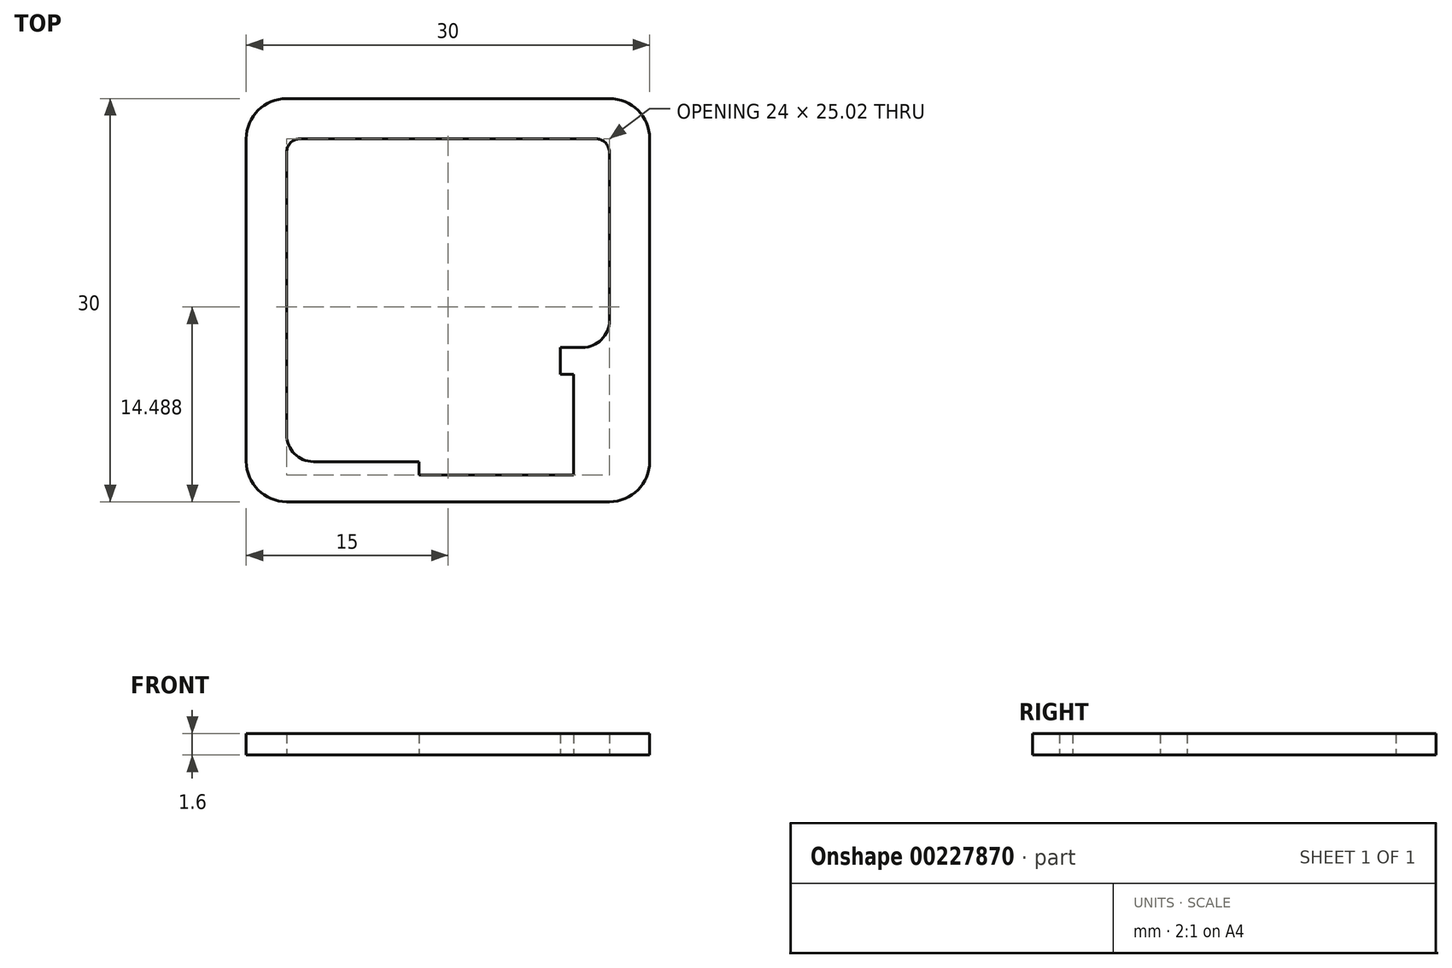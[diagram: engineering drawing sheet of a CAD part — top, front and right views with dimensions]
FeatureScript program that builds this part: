
annotation { "Feature Type Name" : "Feature", "Feature Type Description" : "" }
export const myFeature = defineFeature(function(context is Context, id is Id, definition is map)
    precondition{}
    {
        {
            var Q0;
            Q0=qCreatedBy(makeId("Top.planeOp"),FACE);
            var sketch = newSketch(context, id + "F0", { "sketchPlane" : qUnion([Q0])});
            skLineSegment(sketch, "E0.bottom", {"start": v(12, 15) * mm, "end": v(-12, 15) * mm});
            skLineSegment(sketch, "E0.top", {"start": v(12, -15) * mm, "end": v(-12, -15) * mm});
            skLineSegment(sketch, "E0.left", {"start": v(15, 12) * mm, "end": v(15, -12) * mm});
            skLineSegment(sketch, "E0.right", {"start": v(-15, 12) * mm, "end": v(-15, -12) * mm});
            skPoint(sketch, "E0.middle", {"position": v(0, 0) * mm});
            skPoint(sketch, "E1.visualSharp", {"position": v(-15, 15) * mm});
            skArc(sketch, "E1.filletArc", {"start": v(-12, 15) * mm, "mid": v(-14.12, 14.12) * mm, "end": v(-15, 12) * mm});
            skPoint(sketch, "E2.visualSharp", {"position": v(15, 15) * mm});
            skArc(sketch, "E2.filletArc", {"start": v(15, 12) * mm, "mid": v(14.12, 14.12) * mm, "end": v(12, 15) * mm});
            skPoint(sketch, "E3.visualSharp", {"position": v(15, -15) * mm});
            skArc(sketch, "E3.filletArc", {"start": v(12, -15) * mm, "mid": v(14.12, -14.12) * mm, "end": v(15, -12) * mm});
            skPoint(sketch, "E4.visualSharp", {"position": v(-15, -15) * mm});
            skArc(sketch, "E4.filletArc", {"start": v(-15, -12) * mm, "mid": v(-14.12, -14.12) * mm, "end": v(-12, -15) * mm});
            skPoint(sketch, "E5.middle", {"position": v(0, -0.17) * mm});
            skLineSegment(sketch, "E6.bottom", {"start": v(-2.15, -13.03) * mm, "end": v(9.35, -13.03) * mm});
            skLineSegment(sketch, "E6.top", {"start": v(8.35, -5.53) * mm, "end": v(9.35, -5.53) * mm});
            skLineSegment(sketch, "E6.left", {"start": v(-2.15, -13.03) * mm, "end": v(-2.15, -12.03) * mm});
            skLineSegment(sketch, "E6.right", {"start": v(9.35, -13.03) * mm, "end": v(9.35, -5.53) * mm});
            skLineSegment(sketch, "E7.bottom", {"start": v(-11, 12) * mm, "end": v(11, 12) * mm});
            skLineSegment(sketch, "E7.top", {"start": v(-10, -12.03) * mm, "end": v(-2.15, -12.03) * mm});
            skLineSegment(sketch, "E7.left", {"start": v(-12, 11) * mm, "end": v(-12, -10.03) * mm});
            skLineSegment(sketch, "E7.right", {"start": v(8.35, -3.53) * mm, "end": v(8.35, -5.53) * mm});
            skLineSegment(sketch, "E8", {"start": v(8.35, -5.53) * mm, "end": v(8.35, -3.53) * mm});
            skLineSegment(sketch, "E9", {"start": v(8.35, -3.53) * mm, "end": v(10, -3.53) * mm});
            skLineSegment(sketch, "E10", {"start": v(12, -1.53) * mm, "end": v(12, 11) * mm});
            skPoint(sketch, "E11.visualSharp", {"position": v(12, -3.53) * mm});
            skArc(sketch, "E11.filletArc", {"start": v(10, -3.53) * mm, "mid": v(11.41, -2.94) * mm, "end": v(12, -1.53) * mm});
            skPoint(sketch, "E12.visualSharp", {"position": v(-12, -12.03) * mm});
            skArc(sketch, "E12.filletArc", {"start": v(-12, -10.03) * mm, "mid": v(-11.41, -11.44) * mm, "end": v(-10, -12.03) * mm});
            skArc(sketch, "E13", {"start": v(-11, 12) * mm, "mid": v(-11.7, 11.7) * mm, "end": v(-12, 11) * mm});
            skArc(sketch, "E14", {"start": v(12, 11) * mm, "mid": v(11.7, 11.7) * mm, "end": v(11, 12) * mm});
            skSolve(sketch);
        }
        {
            var Q0;
            Q0=makeQuery(id+"F0.imprint","IMPRINT",FACE,{"disambiguationData":[TD([[makeQuery(id+"F0.imprint","IMPRINT",EDGE,{"derivedFrom":sQuery(id+"F0.wireOp",EDGE,"E0.bottom")}),1.0]])]});
            var Q1;
            Q1=makeQuery(id+"F0.imprint","IMPRINT",FACE,{"disambiguationData":[TD([[makeQuery(id+"F0.imprint","IMPRINT",EDGE,{"derivedFrom":sQuery(id+"F0.wireOp",EDGE,"37d6cbd4-4a48-45da-a80f-8b9b84353664")}),-1.0]])]});
            var Q2;
            {var subQ0=sQuery(id+"F0.wireOp",EDGE,"756c47a4-f17b-4714-afab-c32c89d008be.bottom");Q2=makeQuery(id+"F0.imprint","IMPRINT",FACE,{"disambiguationData":[TD([[makeQuery(id+"F0.imprint","IMPRINT",EDGE,{"derivedFrom":subQ0}),1.0]])]});}
            var Q3;
            {var subQ9=sQuery(id+"F0.wireOp",EDGE,"756c47a4-f17b-4714-afab-c32c89d008be.bottom");Q3=makeQuery(id+"F0.imprint","IMPRINT",FACE,{"disambiguationData":[TD([[makeQuery(id+"F0.imprint","IMPRINT",EDGE,{"derivedFrom":subQ9}),-1.0]])]});}
            extrude(context, id + "F1", {"entities" : qUnion([Q0, Q1, Q2, Q3]), "depth" : 1.6 * mm});
        }
    });
